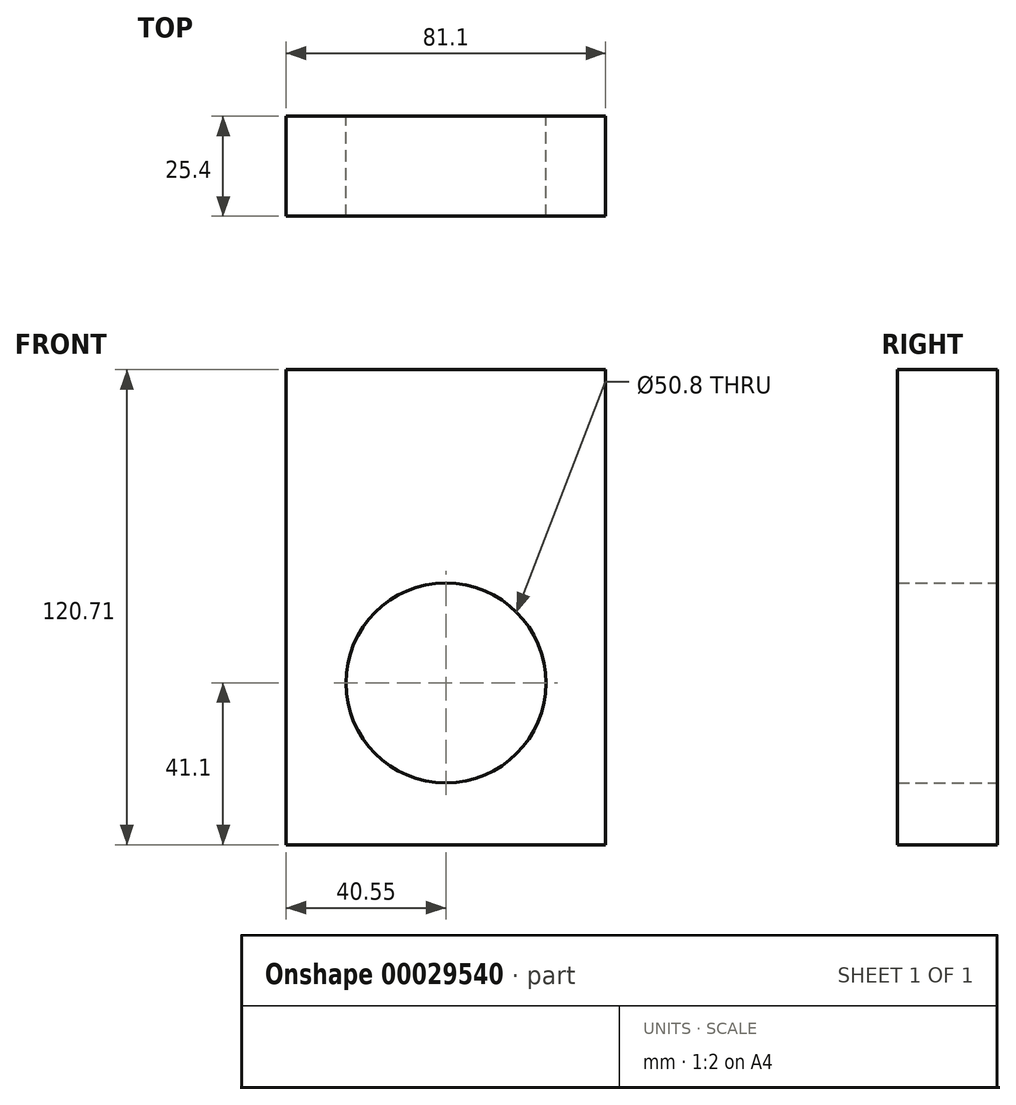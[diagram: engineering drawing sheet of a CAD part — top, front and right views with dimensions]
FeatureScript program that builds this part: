
annotation { "Feature Type Name" : "Feature", "Feature Type Description" : "" }
export const myFeature = defineFeature(function(context is Context, id is Id, definition is map)
    precondition{}
    {
        {
            var Q0;
            Q0=qCreatedBy(makeId("Front.planeOp"),FACE);
            var sketch = newSketch(context, id + "F0", { "sketchPlane" : qUnion([Q0])});
            skCircle(sketch, "E0", {"center": v(0, -2.1) * mm, "radius": 25.4 * mm});
            skLineSegment(sketch, "E1.rect.bottom", {"start": v(40.55, 77.51) * mm, "end": v(-40.55, 77.51) * mm});
            skLineSegment(sketch, "E1.rect.left", {"start": v(40.55, 77.51) * mm, "end": v(40.55, -43.2) * mm});
            skLineSegment(sketch, "E1.rect.right", {"start": v(-40.55, 77.51) * mm, "end": v(-40.55, -43.2) * mm});
            skPoint(sketch, "E1.rect.middle", {"position": v(0, 0) * mm});
            skLineSegment(sketch, "E2", {"start": v(-40.55, -43.2) * mm, "end": v(40.55, -43.2) * mm});
            skPoint(sketch, "E1.rect.top.end.orphan", {"position": v(-40.55, -77.51) * mm});
            skPoint(sketch, "E3.orphan", {"position": v(40.55, -77.51) * mm});
            skSolve(sketch);
        }
        {
            var Q0;
            Q0 = qSketchRegion(id + "F0", true);
            extrude(context, id + "F1", {"entities" : qUnion([Q0]), "depth" : 25.4 * mm});
        }
    });
